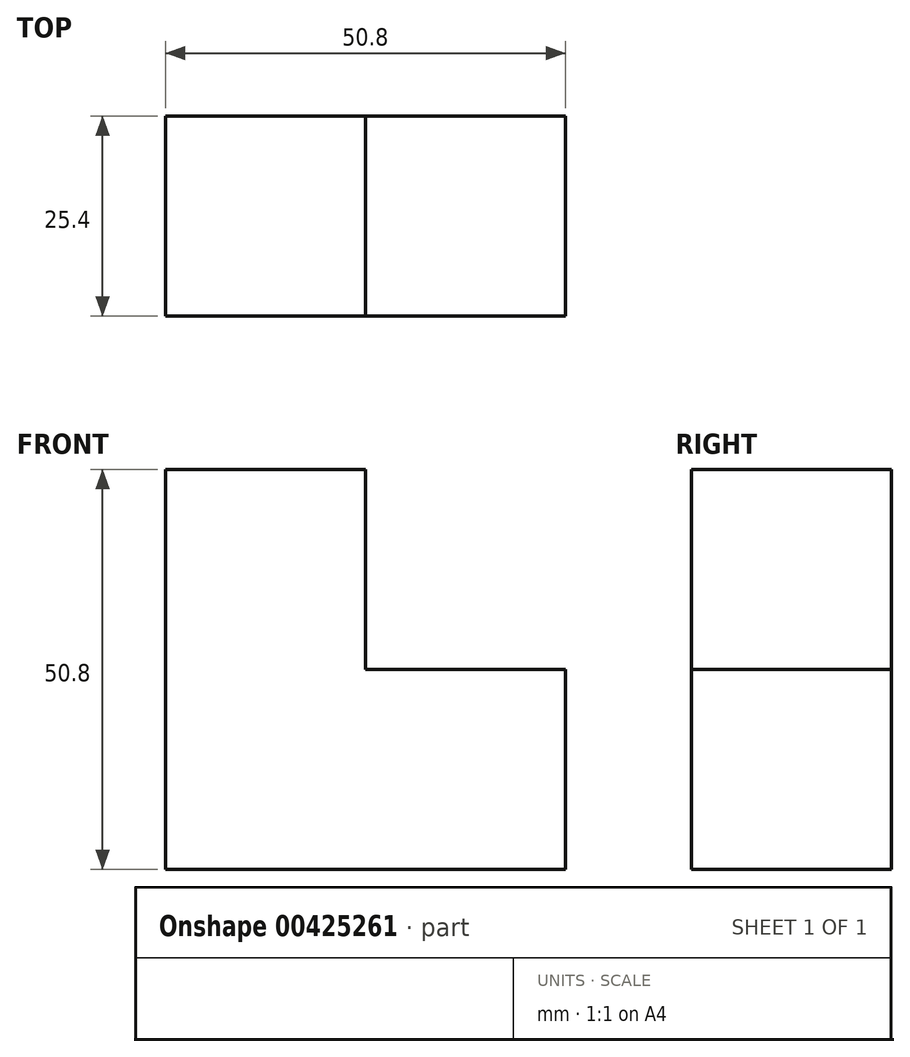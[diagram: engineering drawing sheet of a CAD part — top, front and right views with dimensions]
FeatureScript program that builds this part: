
annotation { "Feature Type Name" : "Feature", "Feature Type Description" : "" }
export const myFeature = defineFeature(function(context is Context, id is Id, definition is map)
    precondition{}
    {
        {
            var Q0;
            Q0=qCreatedBy(makeId("Front.planeOp"),FACE);
            var sketch = newSketch(context, id + "F0", { "sketchPlane" : qUnion([Q0])});
            skLineSegment(sketch, "E0", {"start": v(-45.64, 59.77) * mm, "end": v(-45.64, 8.97) * mm});
            skLineSegment(sketch, "E1", {"start": v(-45.64, 8.97) * mm, "end": v(5.16, 8.97) * mm});
            skLineSegment(sketch, "E2", {"start": v(-45.64, 59.77) * mm, "end": v(-20.24, 59.77) * mm});
            skLineSegment(sketch, "E3", {"start": v(-20.24, 59.77) * mm, "end": v(-20.24, 34.37) * mm});
            skLineSegment(sketch, "E4", {"start": v(-20.24, 34.37) * mm, "end": v(5.16, 34.37) * mm});
            skLineSegment(sketch, "E5", {"start": v(5.16, 34.37) * mm, "end": v(5.16, 8.97) * mm});
            skSolve(sketch);
        }
        {
            var Q0;
            Q0=makeQuery(id+"F0.imprint","IMPRINT",FACE,{"disambiguationData":[TD([[makeQuery(id+"F0.imprint","IMPRINT",EDGE,{"derivedFrom":sQuery(id+"F0.wireOp",EDGE,"E0")}),1.0]])]});
            extrude(context, id + "F1", {"entities" : qUnion([Q0]), "depth" : 25.4 * mm});
        }
    });
